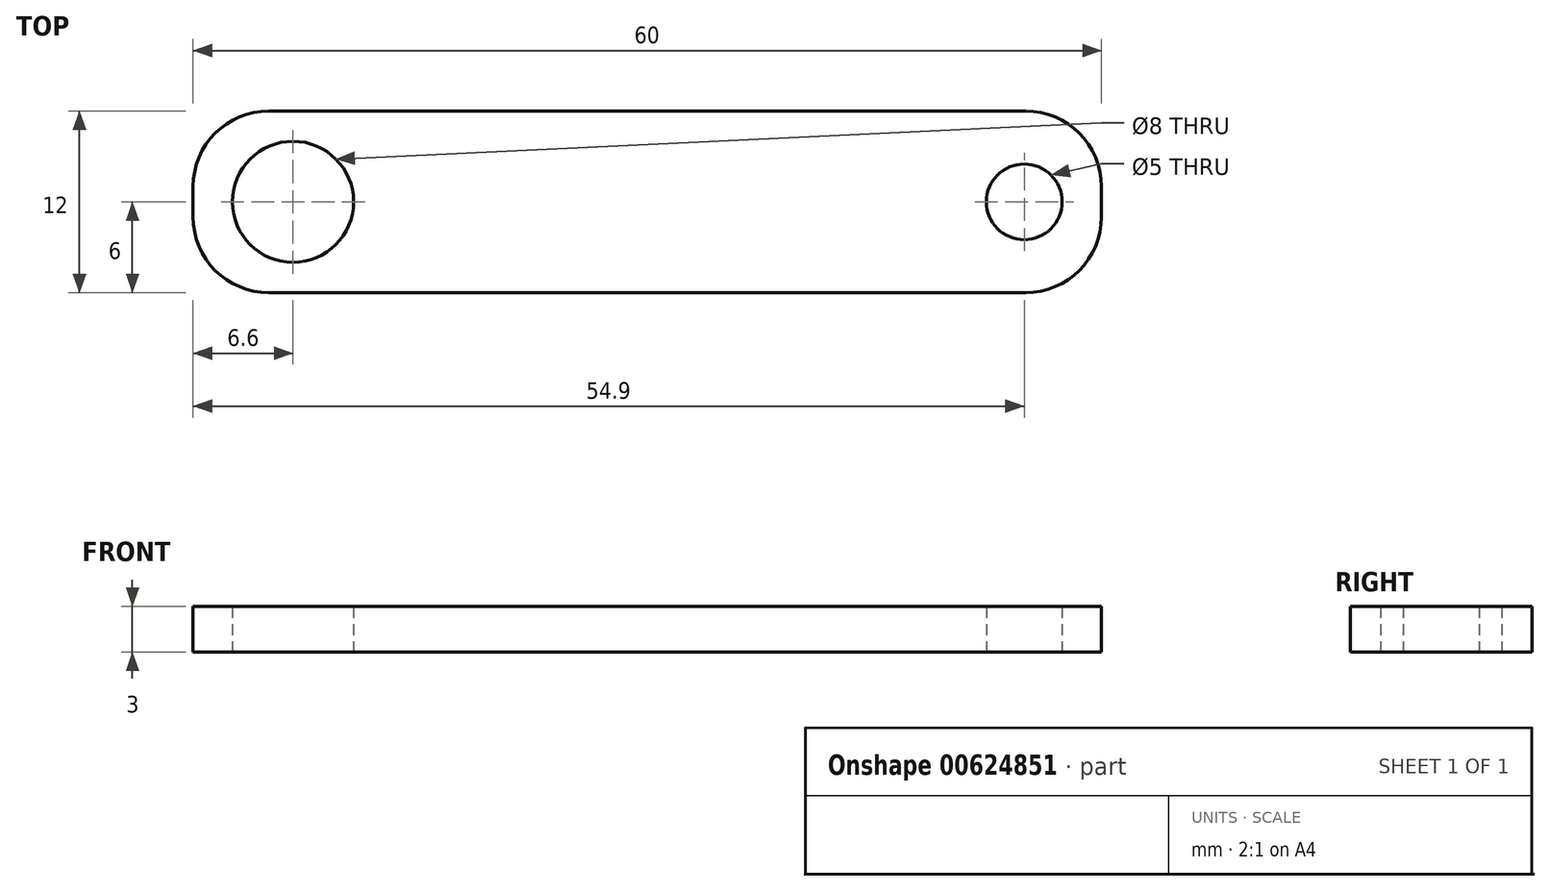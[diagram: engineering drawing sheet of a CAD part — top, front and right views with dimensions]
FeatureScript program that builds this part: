
annotation { "Feature Type Name" : "Feature", "Feature Type Description" : "" }
export const myFeature = defineFeature(function(context is Context, id is Id, definition is map)
    precondition{}
    {
        {
            var Q0;
            Q0=qCreatedBy(makeId("Top.planeOp"),FACE);
            var sketch = newSketch(context, id + "F0", { "sketchPlane" : qUnion([Q0])});
            skLineSegment(sketch, "E0.bottom", {"start": v(5, 0) * mm, "end": v(55, 0) * mm});
            skLineSegment(sketch, "E0.top", {"start": v(5, 12) * mm, "end": v(55, 12) * mm});
            skLineSegment(sketch, "E0.left", {"start": v(0, 5) * mm, "end": v(0, 7) * mm});
            skLineSegment(sketch, "E0.right", {"start": v(60, 5) * mm, "end": v(60, 7) * mm});
            skCircle(sketch, "E1", {"center": v(6.6, 6) * mm, "radius": 4 * mm});
            skCircle(sketch, "E2", {"center": v(54.9, 6) * mm, "radius": 2.5 * mm});
            skPoint(sketch, "E3.visualSharp", {"position": v(0, 12) * mm});
            skArc(sketch, "E3.filletArc", {"start": v(5, 12) * mm, "mid": v(1.46, 10.54) * mm, "end": v(0, 7) * mm});
            skPoint(sketch, "E4.visualSharp", {"position": v(0, 0) * mm});
            skArc(sketch, "E4.filletArc", {"start": v(0, 5) * mm, "mid": v(1.46, 1.46) * mm, "end": v(5, 0) * mm});
            skPoint(sketch, "E5.visualSharp", {"position": v(60, 12) * mm});
            skArc(sketch, "E5.filletArc", {"start": v(60, 7) * mm, "mid": v(58.54, 10.54) * mm, "end": v(55, 12) * mm});
            skPoint(sketch, "E6.visualSharp", {"position": v(60, 0) * mm});
            skArc(sketch, "E6.filletArc", {"start": v(55, 0) * mm, "mid": v(58.54, 1.46) * mm, "end": v(60, 5) * mm});
            skSolve(sketch);
        }
        {
            var Q0;
            Q0 = qSketchRegion(id + "F0", true);
            extrude(context, id + "F1", {"entities" : qUnion([Q0]), "depth" : 3 * mm, "offsetDistance" : 25 * mm});
        }
    });
